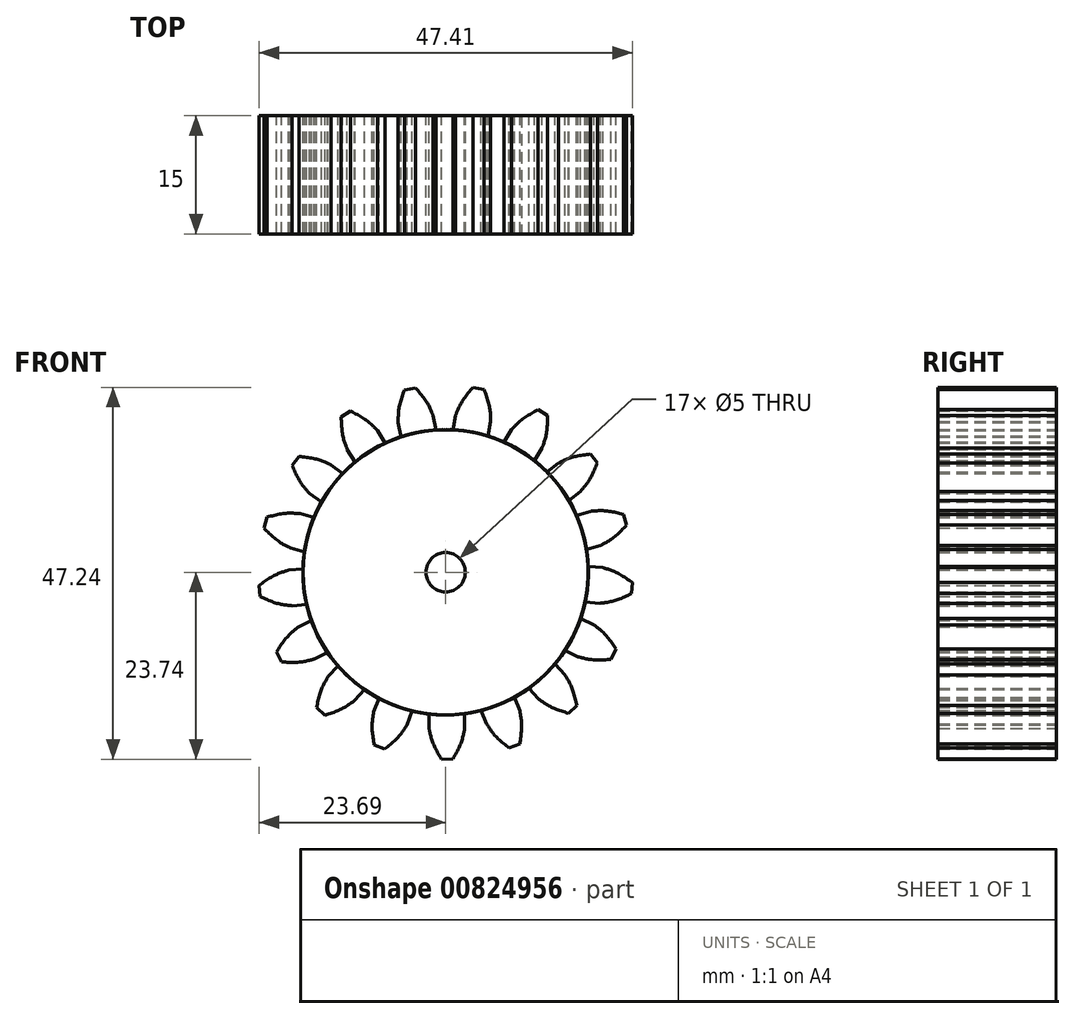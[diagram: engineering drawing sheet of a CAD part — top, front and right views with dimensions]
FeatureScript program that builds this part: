
annotation { "Feature Type Name" : "Feature", "Feature Type Description" : "" }
export const myFeature = defineFeature(function(context is Context, id is Id, definition is map)
    precondition{}
    {
        {
            var Q0;
            Q0=qCreatedBy(makeId("Front.planeOp"),FACE);
            var sketch = newSketch(context, id + "F0", { "sketchPlane" : qUnion([Q0])});
            skCircle(sketch, "E0", {"center": v(0, 0) * mm, "radius": 21.25 * mm, "construction": true});
            skCircle(sketch, "E1", {"center": v(0, 0) * mm, "radius": 23.75 * mm, "construction": true});
            skCircle(sketch, "E2", {"center": v(0, 0) * mm, "radius": 18.13 * mm});
            skCircle(sketch, "E3", {"center": v(0, 0) * mm, "radius": 19.97 * mm, "construction": true});
            skPoint(sketch, "E4", {"position": v(0, 21.25) * mm});
            skLineSegment(sketch, "E5", {"start": v(6.83, 18.76) * mm, "end": v(-5.25, 23.16) * mm, "construction": true});
            skLineSegment(sketch, "E6", {"start": v(-5.25, 23.16) * mm, "end": v(0, 0) * mm, "construction": true});
            skLineSegment(sketch, "E7", {"start": v(6.83, 18.76) * mm, "end": v(0, 0) * mm, "construction": true});
            skLineSegment(sketch, "E8", {"start": v(-6.03, 19.04) * mm, "end": v(0, 0) * mm, "construction": true});
            skPoint(sketch, "E9", {"position": v(-6.03, 19.04) * mm});
            skLineSegment(sketch, "E10", {"start": v(0, 0) * mm, "end": v(3.68, 19.63) * mm, "construction": true});
            skLineSegment(sketch, "E11", {"start": v(0, 0) * mm, "end": v(0.42, 19.96) * mm, "construction": true});
            skLineSegment(sketch, "E12", {"start": v(0, 0) * mm, "end": v(-2.84, 19.77) * mm, "construction": true});
            skLineSegment(sketch, "E13", {"start": v(3.68, 19.63) * mm, "end": v(-5.8, 21.4) * mm, "construction": true});
            skLineSegment(sketch, "E14", {"start": v(0.42, 19.96) * mm, "end": v(-6, 20.1) * mm, "construction": true});
            skLineSegment(sketch, "E15", {"start": v(-2.84, 19.77) * mm, "end": v(-6.02, 19.3) * mm, "construction": true});
            skFitSpline(sketch, "E16", {"points": [v(-6.03, 19.04) * mm, v(-6.02, 19.3) * mm, v(-6, 20.1) * mm, v(-5.8, 21.4) * mm, v(-5.25, 23.16) * mm], "startDerivative": vector(0.05, 1.79) * mm, "endDerivative": vector(1.8, 5.21) * mm});
            skLineSegment(sketch, "E17", {"start": v(0, 0) * mm, "end": v(-5.02, 25.7) * mm, "construction": true});
            skLineSegment(sketch, "E18", {"start": v(0, 0) * mm, "end": v(-5.98, 20.4) * mm, "construction": true});
            skLineSegment(sketch, "E19", {"start": v(-6.03, 19.04) * mm, "end": v(-5.67, 17.22) * mm});
            skFitSpline(sketch, "E20.MirrorCS", {"points": [v(-1.58, 19.9) * mm, v(-1.68, 20.16) * mm, v(-2, 20.88) * mm, v(-2.67, 22.01) * mm, v(-3.84, 23.44) * mm], "startDerivative": vector(-0.72, 1.64) * mm, "endDerivative": vector(-3.62, 4.16) * mm});
            skLineSegment(sketch, "E21.MirrorCS", {"start": v(-1.58, 19.9) * mm, "end": v(-1.22, 18.08) * mm});
            skFitSpline(sketch, "E22", {"points": [v(-5.25, 23.16) * mm, v(-3.84, 23.44) * mm], "startDerivative": vector(1.4, 0.27) * mm, "endDerivative": vector(1.4, 0.27) * mm});
            skSolve(sketch);
        }
        {
            var Q0;
            {var subQ0=sQuery(id+"F0.wireOp",EDGE,"E16");Q0=makeQuery(id+"F0.imprint","IMPRINT",FACE,{"disambiguationData":[TD([[makeQuery(id+"F0.imprint","IMPRINT",EDGE,{"derivedFrom":subQ0}),-1.0]])]});}
            extrude(context, id + "F1", {"entities" : qUnion([Q0]), "depth" : 15 * mm, "offsetDistance" : 25 * mm});
        }
        {
            var Q0;
            Q0 = qSketchRegion(id + "F0", true);
            extrude(context, id + "F2", {"entities" : qUnion([Q0]), "operationType" : NewBodyOperationType.ADD, "depth" : 15 * mm, "offsetDistance" : 25 * mm});
        }
        {
            var Q0;
            Q0=qCreatedBy(makeId("Right.planeOp"),FACE);
            var sketch = newSketch(context, id + "F3", { "sketchPlane" : qUnion([Q0])});
            skLineSegment(sketch, "E23", {"start": v(-64.46, 0) * mm, "end": v(0, 0) * mm});
            skSolve(sketch);
        }
        {
            var Q0;
            Q0=makeQuery(id+"F1.opExtrude","SWEPT_BODY",BODY,{"disambiguationData":[OSD([sQuery(id+"F0.wireOp",EDGE,"E2"),sQuery(id+"F0.wireOp",EDGE,"E16"),sQuery(id+"F0.wireOp",EDGE,"E19"),sQuery(id+"F0.wireOp",EDGE,"E20.MirrorCS"),sQuery(id+"F0.wireOp",EDGE,"E21.MirrorCS"),sQuery(id+"F0.wireOp",EDGE,"E22")])]});
            var Q1;
            Q1=sQuery(id+"F3.wireOp",EDGE,"E23");
            circularPattern(context, id + "F4", {"entities" : qUnion([Q0]), "axis" : qUnion([Q1]), "angle" : 360 * degree, "instanceCount" : 17, "equalSpace" : true});
        }
        {
            var Q0;
            Q0=qCreatedBy(makeId("Front.planeOp"),FACE);
            var sketch = newSketch(context, id + "F5", { "sketchPlane" : qUnion([Q0])});
            skCircle(sketch, "E24", {"center": v(0, 0) * mm, "radius": 2.5 * mm});
            skSolve(sketch);
        }
        {
            var Q0;
            Q0 = qSketchRegion(id + "F5", true);
            extrude(context, id + "F6", {"entities" : qUnion([Q0]), "operationType" : NewBodyOperationType.REMOVE, "endBound" : BoundingType.THROUGH_ALL, "depth" : 25 * mm, "offsetDistance" : 25 * mm});
        }
    });
